# Revit family: Andreu World_Couve_SF-1279
name_source: partatom
category: Mobiliario
revit_build: Autodesk Revit 2014 (Build: 20130722_2115(x64)
units: mm (PartAtom-declared; Revit-internal decimal feet)

## types (1)
- SF-1279
    Arm = 73 mm
    Arm height = 575 mm
    Descripción = 3-seater sofa
    Fabricante = Andreu World
    Height = 675 mm  [stored 2.21457 ft]
    Legs Height = 251 mm  [stored 0.823491 ft]
    Legs Material = Andreu World Polished Aluminum
    Length = 1975 mm  [stored 6.47966 ft]
    Modelo = Couve
    Reference = SF-1279
    Seat Height = 420 mm  [stored 1.37795 ft]
    Seat Length = 1829 mm  [stored 6.00066 ft]
    Seat Material = Andreu World Fabric
    Seat Width = 655 mm  [stored 2.14895 ft]
    URL = http://www.andreuworld.com
    Width = 800 mm  [stored 2.62467 ft]

note: [stored X ft] marks values corroborated as IEEE doubles in the binary element streams (Revit-internal decimal feet)

## geometry (parser evidence)
native form markers: Blend x13, Sweep x1
no freeform markers — native parametric forms only
